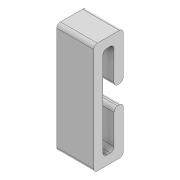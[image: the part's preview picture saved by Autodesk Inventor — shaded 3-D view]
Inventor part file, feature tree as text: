
AUTODESK INVENTOR PART (.ipt)
format: ipt  version: 2020 (Build 240168000, 168)  size: 114,176 bytes
history: native  units: mm
features: other x1, extrude x1, sketch x1
ambient origin geometry x8: Origin, YZ Plane, XZ Plane, XY Plane, X Axis, Y Axis, Z Axis, Center Point
bodies: Body1 (feature_tree)
feature tree (3):
  other  "Твердое тело1"
  extrude  "Выдавливание1"  Depth=25.0mm
  sketch  "Эскиз1"
